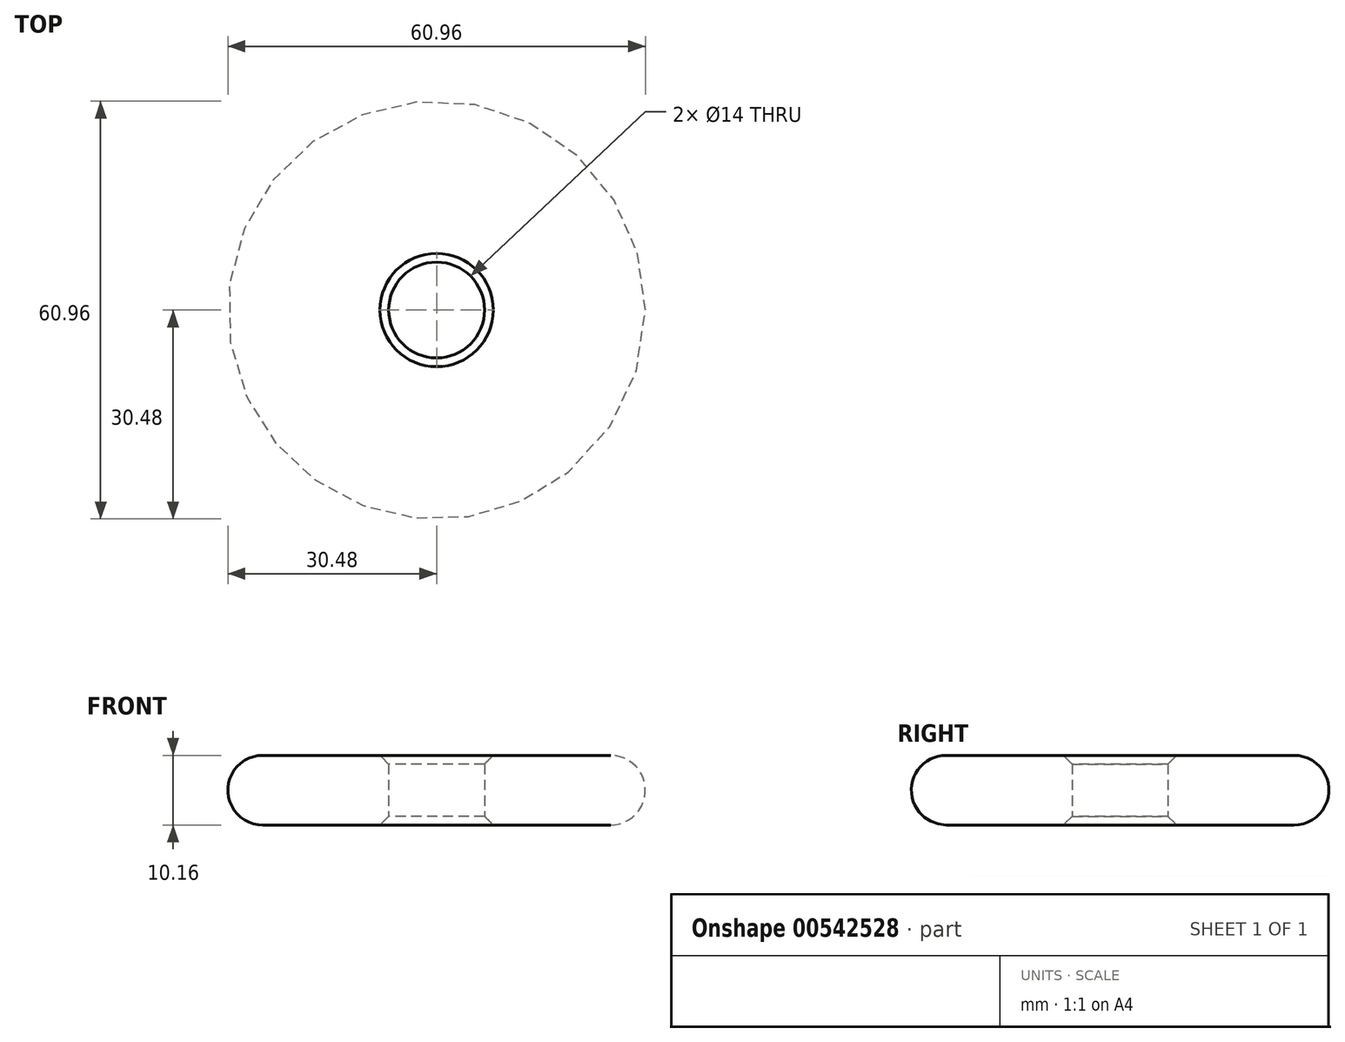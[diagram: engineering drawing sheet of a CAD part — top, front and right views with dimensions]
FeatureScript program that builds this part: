
annotation { "Feature Type Name" : "Feature", "Feature Type Description" : "" }
export const myFeature = defineFeature(function(context is Context, id is Id, definition is map)
    precondition{}
    {
        {
            var Q0;
            Q0=qCreatedBy(makeId("Top.planeOp"),FACE);
            var sketch = newSketch(context, id + "F0", { "sketchPlane" : qUnion([Q0])});
            skCircle(sketch, "E0", {"center": v(0, 0) * mm, "radius": 30.48 * mm});
            skCircle(sketch, "E1", {"center": v(0, 0) * mm, "radius": 7 * mm});
            skSolve(sketch);
        }
        {
            var Q0;
            Q0=makeQuery(id+"F0.imprint","IMPRINT",FACE,{"disambiguationData":[TD([[makeQuery(id+"F0.imprint","IMPRINT",EDGE,{"derivedFrom":sQuery(id+"F0.wireOp",EDGE,"E0")}),1.0]])]});
            extrude(context, id + "F1", {"entities" : qUnion([Q0]), "depth" : 10.16 * mm, "offsetDistance" : 25.4 * mm});
        }
        {
            var Q0;
            Q0=makeQuery(id+"F1.opExtrude","CAP_EDGE",EDGE,{"disambiguationData":[OSD([sQuery(id+"F0.wireOp",EDGE,"E0")])],"isStart":false});
            var Q1;
            Q1=makeQuery(id+"F1.opExtrude","CAP_EDGE",EDGE,{"disambiguationData":[OSD([sQuery(id+"F0.wireOp",EDGE,"E0")])],"isStart":true});
            fillet(context, id + "F2", {"entities" : qUnion([Q0, Q1]), "radius" : 5.08 * mm, "tangentPropagation" : true, "allowEdgeOverflow" : false});
        }
        {
            var Q0;
            Q0=makeQuery(id+"F1.opExtrude","CAP_EDGE",EDGE,{"disambiguationData":[OSD([sQuery(id+"F0.wireOp",EDGE,"E1")])],"isStart":false});
            var Q1;
            Q1=makeQuery(id+"F1.opExtrude","CAP_EDGE",EDGE,{"disambiguationData":[OSD([sQuery(id+"F0.wireOp",EDGE,"E1")])],"isStart":true});
            chamfer(context, id + "F3", {"entities" : qUnion([Q0, Q1]), "width" : 1.27 * mm, "tangentPropagation" : true});
        }
    });
